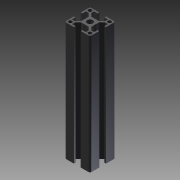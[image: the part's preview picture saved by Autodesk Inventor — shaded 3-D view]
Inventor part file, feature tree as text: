
AUTODESK INVENTOR PART (.ipt)
format: ipt  version: 2011 SP1 (Build 150282100, 282)  size: 190,464 bytes
history: native  units: mm
features: other x21, sketch x3, hole x2, extrude x1, pattern_linear x1
ambient origin geometry x8: Origin, YZ Plane, XZ Plane, XY Plane, X Axis, Y Axis, Z Axis, Center Point
bodies: Solid1 (feature_tree)
feature tree (28):
  extrude  "Extrusion1"  Depth=20.0mm
  hole  "Hole1"  [1 undecoded]
  hole  "Hole2"  [1 undecoded]
  pattern_linear  "Rectangular Pattern1"  [2 undecoded]
  other  "C1_XY"
  other  "C1_YZ"
  other  "C1_ZX"
  other  "C1_X"
  other  "C1_Y"
  other  "C1_Z"
  other  "C1_Center"
  other  "to_frame_cap1_XY"
  other  "to_frame_cap1_YZ"
  other  "to_frame_cap1_ZX"
  other  "to_frame_cap1_X"
  other  "to_frame_cap1_Y"
  other  "to_frame_cap1_Z"
  other  "to_frame_cap1_Center"
  other  "to_frame_cap2_XY"
  other  "to_frame_cap2_YZ"
  other  "to_frame_cap2_ZX"
  other  "to_frame_cap2_X"
  other  "to_frame_cap2_Y"
  other  "to_frame_cap2_Z"
  other  "to_frame_cap2_Center"
  sketch  "Sketch_1"  dims[d0=140.0mm d1=0.0mm]
  sketch  "Sketch2"  dims[d2=6.8mm d3=6.0mm d4=4.0mm d5=2.0mm d6=90.0deg d7=140.0mm d8=0.0mm]
  sketch  "Sketch3"  dims[d9=4.2mm d10=6.0mm d11=4.0mm d12=2.0mm d13=90.0deg d14=140.0mm d15=0.0mm d16=20.0mm d18=23.2mm d19=20.0mm d21=23.2mm d22=0.0mm d23=0.0mm d24=0.0mm]
note: 4 required parameter values undecoded (feature->parameter linkage not recoverable at this tier; creation-order binding heuristic only, values carry confidence <= 0.55)
